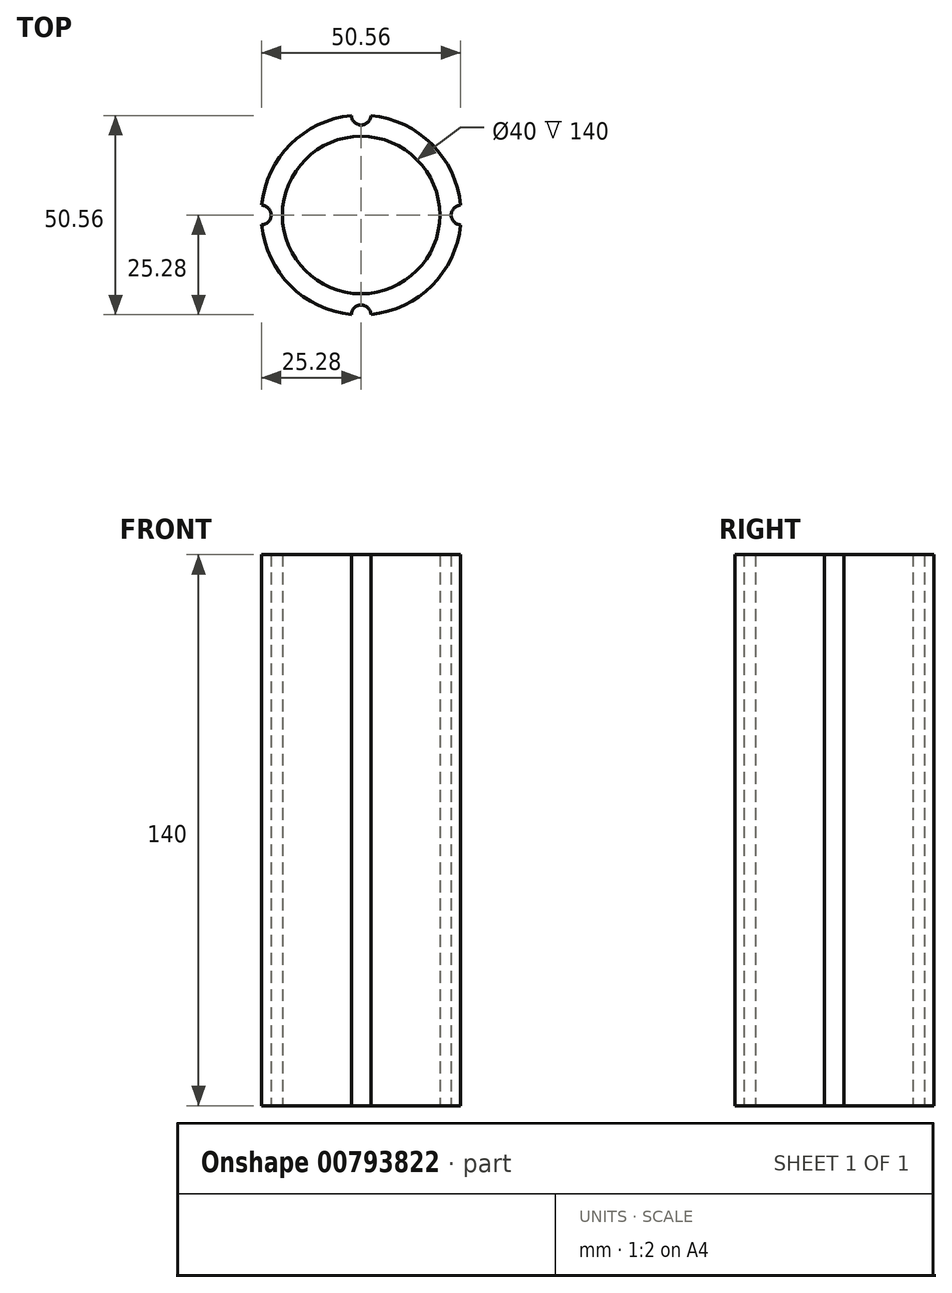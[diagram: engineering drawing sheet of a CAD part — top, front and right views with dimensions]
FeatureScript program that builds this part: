
annotation { "Feature Type Name" : "Feature", "Feature Type Description" : "" }
export const myFeature = defineFeature(function(context is Context, id is Id, definition is map)
    precondition{}
    {
        {
            var Q0;
            Q0=qCreatedBy(makeId("Top.planeOp"),FACE);
            var sketch = newSketch(context, id + "F0", { "sketchPlane" : qUnion([Q0])});
            skCircle(sketch, "E0", {"center": v(0, 0) * mm, "radius": 25.4 * mm});
            skCircle(sketch, "E1", {"center": v(0, 0) * mm, "radius": 20 * mm});
            skArc(sketch, "E2", {"start": v(25.28, 2.5) * mm, "mid": v(22.89, 0) * mm, "end": v(25.28, -2.5) * mm});
            skArc(sketch, "E3", {"start": v(2.5, -25.28) * mm, "mid": v(0, -22.88) * mm, "end": v(-2.5, -25.28) * mm});
            skArc(sketch, "E4", {"start": v(-2.5, 25.28) * mm, "mid": v(0, 22.88) * mm, "end": v(2.5, 25.28) * mm});
            skArc(sketch, "E5", {"start": v(-25.28, -2.5) * mm, "mid": v(-22.87, 0) * mm, "end": v(-25.28, 2.5) * mm});
            skSolve(sketch);
        }
        {
            var Q0;
            Q0=makeQuery(id+"F0.imprint","IMPRINT",FACE,{"disambiguationData":[TD([[makeQuery(id+"F0.imprint","IMPRINT",EDGE,{"derivedFrom":sQuery(id+"F0.wireOp",EDGE,"E0")}),1.0]])]});
            extrude(context, id + "F1", {"entities" : qUnion([Q0]), "depth" : 140 * mm, "offsetDistance" : 25.4 * mm});
        }
    });
